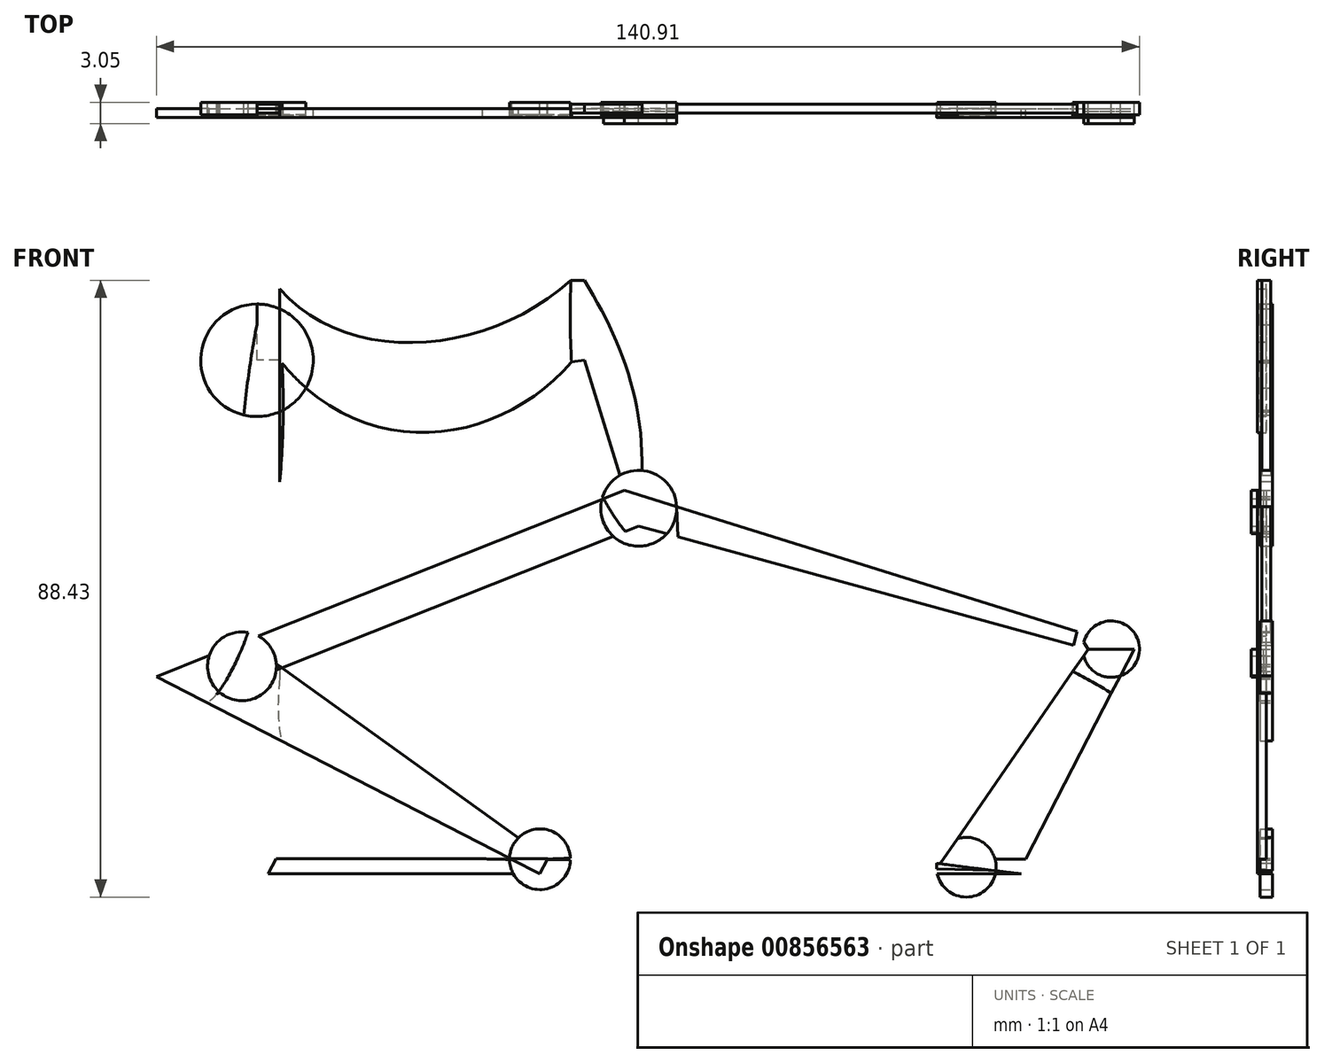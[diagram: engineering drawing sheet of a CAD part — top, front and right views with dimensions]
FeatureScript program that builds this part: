
annotation { "Feature Type Name" : "Feature", "Feature Type Description" : "" }
export const myFeature = defineFeature(function(context is Context, id is Id, definition is map)
    precondition{}
    {
        {
            var Q0;
            Q0=qCreatedBy(makeId("Front.planeOp"),FACE);
            var sketch = newSketch(context, id + "F0", { "sketchPlane" : qUnion([Q0])});
            skLineSegment(sketch, "E0", {"start": v(-61.65, 70.37) * mm, "end": v(-61.65, 0) * mm});
            skFitSpline(sketch, "E1", {"points": [v(-61.65, 0) * mm, v(-26.78, -25.9) * mm, v(7.97, -24.21) * mm, v(44.58, -27.97) * mm, v(64.47, -26.74) * mm, v(71.94, -19.1) * mm, v(70.5, -13.3) * mm, v(44.7, 4.15) * mm, v(0, 12.67) * mm, v(-18.49, 35.05) * mm, v(-18.6, 75.27) * mm], "startDerivative": vector(-64.2, -574.15) * mm, "endDerivative": vector(16.77, 189.29) * mm});
            skFitSpline(sketch, "E2", {"points": [v(-61.65, 55.92) * mm, v(-19.91, 57.13) * mm], "startDerivative": vector(29.36, -33.67) * mm, "endDerivative": vector(36.1, 32.54) * mm});
            skFitSpline(sketch, "E3", {"points": [v(-61.65, 45.68) * mm, v(-19.82, 45.43) * mm], "startDerivative": vector(37.74, -46.8) * mm, "endDerivative": vector(29.91, 34.83) * mm});
            skLineSegment(sketch, "E4", {"start": v(-61.65, 45.68) * mm, "end": v(-64.9, 45.68) * mm});
            skLineSegment(sketch, "E5", {"start": v(-64.9, 45.68) * mm, "end": v(-64.9, 55.92) * mm});
            skLineSegment(sketch, "E6", {"start": v(-64.9, 55.92) * mm, "end": v(-61.65, 55.92) * mm});
            skLineSegment(sketch, "E7", {"start": v(-19.91, 57.13) * mm, "end": v(-17.99, 57.13) * mm});
            skLineSegment(sketch, "E8", {"start": v(-17.99, 57.13) * mm, "end": v(-17.99, 45.68) * mm});
            skLineSegment(sketch, "E9", {"start": v(-17.99, 45.68) * mm, "end": v(-19.82, 45.43) * mm});
            skFitSpline(sketch, "E10", {"points": [v(-64.9, 50.8) * mm, v(-79.63, 0) * mm], "startDerivative": vector(-10.54, -51.15) * mm, "endDerivative": vector(-39.02, -39.29) * mm});
            skFitSpline(sketch, "E11", {"points": [v(-61.73, 50.8) * mm, v(-70.66, -2.16) * mm, v(-79.63, 0) * mm], "startDerivative": vector(10.97, -108.7) * mm, "endDerivative": vector(-50.85, 48.8) * mm});
            skLineSegment(sketch, "E12", {"start": v(-70.66, -2.16) * mm, "end": v(-10.18, 21.9) * mm});
            skLineSegment(sketch, "E13", {"start": v(-10.18, 21.9) * mm, "end": v(-12.22, 27.02) * mm});
            skLineSegment(sketch, "E14", {"start": v(-12.22, 27.02) * mm, "end": v(-79.32, 0.32) * mm});
            skLineSegment(sketch, "E15", {"start": v(-79.32, 0.32) * mm, "end": v(-24.34, -27.97) * mm});
            skLineSegment(sketch, "E16", {"start": v(-24.34, -27.97) * mm, "end": v(-23.23, -25.8) * mm});
            skLineSegment(sketch, "E17", {"start": v(-23.23, -25.8) * mm, "end": v(-66.66, 5.36) * mm});
            skLineSegment(sketch, "E18", {"start": v(-23.23, -25.8) * mm, "end": v(-62.17, -25.8) * mm});
            skLineSegment(sketch, "E19", {"start": v(-62.17, -25.8) * mm, "end": v(-63.28, -27.97) * mm});
            skLineSegment(sketch, "E20", {"start": v(-63.28, -27.97) * mm, "end": v(-23.23, -27.97) * mm});
            skLineSegment(sketch, "E21", {"start": v(-23.23, -27.97) * mm, "end": v(60.88, -27.97) * mm});
            skLineSegment(sketch, "E22", {"start": v(60.88, -27.97) * mm, "end": v(-24.34, -25.87) * mm});
            skLineSegment(sketch, "E23", {"start": v(-24.34, -25.87) * mm, "end": v(61.59, -25.87) * mm});
            skLineSegment(sketch, "E24", {"start": v(61.59, -25.87) * mm, "end": v(60.88, -27.97) * mm});
            skLineSegment(sketch, "E25", {"start": v(33.01, -26.53) * mm, "end": v(54.26, 4.25) * mm});
            skLineSegment(sketch, "E26", {"start": v(45.32, -25.87) * mm, "end": v(60.82, 4.25) * mm});
            skLineSegment(sketch, "E27", {"start": v(60.82, 4.25) * mm, "end": v(-12.22, 27.02) * mm});
            skLineSegment(sketch, "E28", {"start": v(-10.18, 21.9) * mm, "end": v(54.26, 4.25) * mm});
            skLineSegment(sketch, "E29", {"start": v(54.26, 4.25) * mm, "end": v(60.82, 4.25) * mm});
            skCircle(sketch, "E30", {"center": v(-67.05, 1.8) * mm, "radius": 4.93 * mm});
            skCircle(sketch, "E31", {"center": v(-10.18, 24.46) * mm, "radius": 5.44 * mm});
            skPoint(sketch, "E31.centerSnap0", {"position": v(-11.2, 24.46) * mm});
            skCircle(sketch, "E32", {"center": v(57.54, 4.25) * mm, "radius": 4.05 * mm});
            skCircle(sketch, "E33", {"center": v(-24.34, -25.87) * mm, "radius": 4.36 * mm});
            skCircle(sketch, "E34", {"center": v(36.78, -27.02) * mm, "radius": 4.28 * mm});
            skCircle(sketch, "E35", {"center": v(-64.9, 45.68) * mm, "radius": 8.06 * mm});
            skFitSpline(sketch, "E36", {"points": [v(-17.99, 57.13) * mm, v(-10.18, 24.46) * mm], "startDerivative": vector(17.67, -28.59) * mm, "endDerivative": vector(-5.48, -39.2) * mm});
            skFitSpline(sketch, "E37", {"points": [v(-17.99, 45.68) * mm, v(-12.22, 27.02) * mm], "startDerivative": vector(5.77, -18.66) * mm, "endDerivative": vector(5.77, -18.66) * mm});
            skLineSegment(sketch, "E38", {"start": v(-4.75, 24.7) * mm, "end": v(-4.56, 20.36) * mm});
            skLineSegment(sketch, "E39", {"start": v(54.26, 4.25) * mm, "end": v(52.66, 6.8) * mm});
            skLineSegment(sketch, "E40", {"start": v(52.66, 6.8) * mm, "end": v(52.12, 4.84) * mm});
            skSolve(sketch);
        }
        {
            var Q0;
            {var subQ5=sQuery(id+"F0.wireOp",EDGE,"E4");Q0=makeQuery(id+"F0.imprint","IMPRINT",FACE,{"disambiguationData":[TD([[makeQuery(id+"F0.imprint","IMPRINT",EDGE,{"derivedFrom":subQ5}),1.0]])]});}
            var Q1;
            {var subQ0=sQuery(id+"F0.wireOp",EDGE,"E2");Q1=makeQuery(id+"F0.imprint","IMPRINT",FACE,{"disambiguationData":[TD([[makeQuery(id+"F0.imprint","IMPRINT",EDGE,{"derivedFrom":subQ0}),-1.0]])]});}
            var Q2;
            {var subQ1=sQuery(id+"F0.wireOp",EDGE,"E4");Q2=makeQuery(id+"F0.imprint","IMPRINT",FACE,{"disambiguationData":[TD([[makeQuery(id+"F0.imprint","IMPRINT",EDGE,{"derivedFrom":subQ1}),-1.0]])]});}
            var Q3;
            {var subQ0=sQuery(id+"F0.wireOp",EDGE,"E14");var subQ1=sQuery(id+"F0.wireOp",EDGE,"E0");var subQ2=makeQuery(id+"F0.imprint","INTERSECT",VERTEX,{"derivedFrom":[subQ1,subQ0]});Q3=makeQuery(id+"F0.imprint","IMPRINT",FACE,{"disambiguationData":[TD([[makeQuery(id+"F0.imprint","IMPRINT",EDGE,{"disambiguationData":[TD([[subQ2,-1.0]])],"derivedFrom":subQ1}),-1.0]])]});}
            var Q4;
            {var subQ0=sQuery(id+"F0.wireOp",EDGE,"E14");var subQ3=sQuery(id+"F0.wireOp",EDGE,"E0");var subQ4=makeQuery(id+"F0.imprint","INTERSECT",VERTEX,{"derivedFrom":[subQ3,subQ0]});Q4=makeQuery(id+"F0.imprint","IMPRINT",FACE,{"disambiguationData":[TD([[makeQuery(id+"F0.imprint","IMPRINT",EDGE,{"disambiguationData":[TD([[subQ4,-1.0]])],"derivedFrom":subQ3}),1.0]])]});}
            var Q5;
            {var subQ1=sQuery(id+"F0.wireOp",EDGE,"E1");var subQ6=sQuery(id+"F0.wireOp",EDGE,"E0");var subQ10=makeQuery(id+"F0.imprint","INTERSECT",VERTEX,{"derivedFrom":[subQ6,subQ1]});Q5=makeQuery(id+"F0.imprint","IMPRINT",FACE,{"disambiguationData":[TD([[makeQuery(id+"F0.imprint","IMPRINT",EDGE,{"disambiguationData":[TD([[subQ10,1.0]])],"derivedFrom":subQ6}),1.0]])]});}
            var Q6;
            {var subQ5=sQuery(id+"F0.wireOp",EDGE,"E1");var subQ6=sQuery(id+"F0.wireOp",EDGE,"E0");var subQ7=makeQuery(id+"F0.imprint","INTERSECT",VERTEX,{"derivedFrom":[subQ6,subQ5]});Q6=makeQuery(id+"F0.imprint","IMPRINT",FACE,{"disambiguationData":[TD([[makeQuery(id+"F0.imprint","IMPRINT",EDGE,{"disambiguationData":[TD([[subQ7,1.0]])],"derivedFrom":subQ6}),-1.0]])]});}
            var Q7;
            {var subQ0=sQuery(id+"F0.wireOp",EDGE,"E11");var subQ1=makeQuery(id+"F0.imprint","INTERSECT",VERTEX,{"derivedFrom":[subQ0,sQuery(id+"F0.wireOp",EDGE,"E12")]});Q7=makeQuery(id+"F0.imprint","IMPRINT",FACE,{"disambiguationData":[TD([[makeQuery(id+"F0.imprint","IMPRINT",EDGE,{"disambiguationData":[TD([[subQ1,-1.0]])],"derivedFrom":subQ0}),-1.0]])]});}
            var Q8;
            Q8=makeQuery(id+"F0.imprint","IMPRINT",FACE,{"disambiguationData":[TD([[makeQuery(id+"F0.imprint","IMPRINT",EDGE,{"derivedFrom":sQuery(id+"F0.wireOp",EDGE,"E13")}),-1.0]])]});
            var Q9;
            {var subQ5=sQuery(id+"F0.wireOp",EDGE,"E13");Q9=makeQuery(id+"F0.imprint","IMPRINT",FACE,{"disambiguationData":[TD([[makeQuery(id+"F0.imprint","IMPRINT",EDGE,{"derivedFrom":subQ5}),1.0]])]});}
            var Q10;
            {var subQ0=sQuery(id+"F0.wireOp",EDGE,"E26");var subQ1=sQuery(id+"F0.wireOp",EDGE,"E1");var subQ2=makeQuery(id+"F0.imprint","INTERSECT",VERTEX,{"derivedFrom":[subQ1,subQ0]});Q10=makeQuery(id+"F0.imprint","IMPRINT",FACE,{"disambiguationData":[TD([[makeQuery(id+"F0.imprint","IMPRINT",EDGE,{"disambiguationData":[TD([[subQ2,-1.0]])],"derivedFrom":subQ1}),1.0]])]});}
            var Q11;
            {var subQ5=sQuery(id+"F0.wireOp",EDGE,"E29");Q11=makeQuery(id+"F0.imprint","IMPRINT",FACE,{"disambiguationData":[TD([[makeQuery(id+"F0.imprint","IMPRINT",EDGE,{"derivedFrom":subQ5}),-1.0]])]});}
            var Q12;
            {var subQ0=sQuery(id+"F0.wireOp",EDGE,"E21");var subQ3=sQuery(id+"F0.wireOp",EDGE,"E1");var subQ4=makeQuery(id+"F0.imprint","INTERSECT",VERTEX,{"derivedFrom":[subQ3,subQ0]});Q12=makeQuery(id+"F0.imprint","IMPRINT",FACE,{"disambiguationData":[TD([[makeQuery(id+"F0.imprint","IMPRINT",EDGE,{"disambiguationData":[TD([[subQ4,1.0]])],"derivedFrom":subQ3}),-1.0]])]});}
            var Q13;
            {var subQ1=sQuery(id+"F0.wireOp",EDGE,"E1");var subQ7=makeQuery(id+"F0.imprint","INTERSECT",VERTEX,{"disambiguationData":[OD(0.0)],"derivedFrom":[subQ1,sQuery(id+"F0.wireOp",EDGE,"E25")]});Q13=makeQuery(id+"F0.imprint","IMPRINT",FACE,{"disambiguationData":[TD([[makeQuery(id+"F0.imprint","IMPRINT",EDGE,{"disambiguationData":[TD([[subQ7,1.0]])],"derivedFrom":subQ1}),-1.0]])]});}
            var Q14;
            {var subQ0=sQuery(id+"F0.wireOp",EDGE,"E19");Q14=makeQuery(id+"F0.imprint","IMPRINT",FACE,{"disambiguationData":[TD([[makeQuery(id+"F0.imprint","IMPRINT",EDGE,{"derivedFrom":subQ0}),1.0]])]});}
            extrude(context, id + "F1", {"entities" : qUnion([Q0, Q1, Q2, Q3, Q4, Q5, Q6, Q7, Q8, Q9, Q10, Q11, Q12, Q13, Q14]), "depth" : 1.27 * mm, "offsetDistance" : 25.4 * mm});
        }
        {
            var Q0;
            {var subQ0=sQuery(id+"F0.wireOp",EDGE,"E38");Q0=makeQuery(id+"F0.imprint","IMPRINT",FACE,{"disambiguationData":[TD([[makeQuery(id+"F0.imprint","IMPRINT",EDGE,{"derivedFrom":subQ0}),1.0]])]});}
            var Q1;
            {var subQ0=sQuery(id+"F0.wireOp",EDGE,"E8");Q1=makeQuery(id+"F0.imprint","IMPRINT",FACE,{"disambiguationData":[TD([[makeQuery(id+"F0.imprint","IMPRINT",EDGE,{"derivedFrom":subQ0}),1.0]])]});}
            var Q2;
            {var subQ0=sQuery(id+"F0.wireOp",EDGE,"E7");Q2=makeQuery(id+"F0.imprint","IMPRINT",FACE,{"disambiguationData":[TD([[makeQuery(id+"F0.imprint","IMPRINT",EDGE,{"derivedFrom":subQ0}),-1.0]])]});}
            var Q3;
            {var subQ6=sQuery(id+"F0.wireOp",EDGE,"E0");var subQ9=sQuery(id+"F0.wireOp",EDGE,"E35");var subQ11=makeQuery(id+"F0.imprint","INTERSECT",VERTEX,{"disambiguationData":[OD(1.0)],"derivedFrom":[subQ6,subQ9]});Q3=makeQuery(id+"F0.imprint","IMPRINT",FACE,{"disambiguationData":[TD([[makeQuery(id+"F0.imprint","IMPRINT",EDGE,{"disambiguationData":[TD([[subQ11,-1.0]])],"derivedFrom":subQ6}),-1.0]])]});}
            extrude(context, id + "F2", {"entities" : qUnion([Q0, Q1, Q2, Q3]), "endBound" : BoundingType.SYMMETRIC, "depth" : 1.27 * mm, "offsetDistance" : 25.4 * mm});
        }
        {
            var Q0;
            {var subQ0=sQuery(id+"F0.wireOp",EDGE,"E10");var subQ1=sQuery(id+"F0.wireOp",EDGE,"E5");var subQ2=makeQuery(id+"F0.imprint","INTERSECT",VERTEX,{"derivedFrom":[subQ1,subQ0]});Q0=makeQuery(id+"F0.imprint","IMPRINT",FACE,{"disambiguationData":[TD([[makeQuery(id+"F0.imprint","IMPRINT",EDGE,{"disambiguationData":[TD([[subQ2,-1.0]])],"derivedFrom":subQ1}),1.0]])]});}
            var Q1;
            {var subQ0=sQuery(id+"F0.wireOp",EDGE,"E11");var subQ1=sQuery(id+"F0.wireOp",EDGE,"E0");var subQ2=makeQuery(id+"F0.imprint","INTERSECT",VERTEX,{"disambiguationData":[OD(0.0)],"derivedFrom":[subQ1,subQ0]});Q1=makeQuery(id+"F0.imprint","IMPRINT",FACE,{"disambiguationData":[TD([[makeQuery(id+"F0.imprint","IMPRINT",EDGE,{"disambiguationData":[TD([[subQ2,1.0]])],"derivedFrom":subQ1}),1.0]])]});}
            var Q2;
            {var subQ0=sQuery(id+"F0.wireOp",EDGE,"E11");var subQ1=sQuery(id+"F0.wireOp",EDGE,"E3");var subQ2=makeQuery(id+"F0.imprint","INTERSECT",VERTEX,{"derivedFrom":[subQ1,subQ0]});Q2=makeQuery(id+"F0.imprint","IMPRINT",FACE,{"disambiguationData":[TD([[makeQuery(id+"F0.imprint","IMPRINT",EDGE,{"disambiguationData":[TD([[subQ2,-1.0]])],"derivedFrom":subQ1}),-1.0]])]});}
            var Q3;
            {var subQ1=sQuery(id+"F0.wireOp",EDGE,"E11");var subQ3=sQuery(id+"F0.wireOp",EDGE,"E30");var subQ4=makeQuery(id+"F0.imprint","INTERSECT",VERTEX,{"disambiguationData":[OD(1.0)],"derivedFrom":[subQ1,subQ3]});Q3=makeQuery(id+"F0.imprint","IMPRINT",FACE,{"disambiguationData":[TD([[makeQuery(id+"F0.imprint","IMPRINT",EDGE,{"disambiguationData":[TD([[subQ4,1.0]])],"derivedFrom":subQ3}),1.0]])]});}
            var Q4;
            {var subQ1=sQuery(id+"F0.wireOp",EDGE,"E11");var subQ3=sQuery(id+"F0.wireOp",EDGE,"E30");var subQ4=makeQuery(id+"F0.imprint","INTERSECT",VERTEX,{"disambiguationData":[OD(0.0)],"derivedFrom":[subQ1,subQ3]});Q4=makeQuery(id+"F0.imprint","IMPRINT",FACE,{"disambiguationData":[TD([[makeQuery(id+"F0.imprint","IMPRINT",EDGE,{"disambiguationData":[TD([[subQ4,-1.0]])],"derivedFrom":subQ3}),1.0]])]});}
            var Q5;
            {var subQ3=sQuery(id+"F0.wireOp",EDGE,"E30");var subQ6=sQuery(id+"F0.wireOp",EDGE,"E12");var subQ7=makeQuery(id+"F0.imprint","INTERSECT",VERTEX,{"disambiguationData":[OD(0.0)],"derivedFrom":[subQ6,subQ3]});Q5=makeQuery(id+"F0.imprint","IMPRINT",FACE,{"disambiguationData":[TD([[makeQuery(id+"F0.imprint","IMPRINT",EDGE,{"disambiguationData":[TD([[subQ7,-1.0]])],"derivedFrom":subQ6}),1.0]])]});}
            var Q6;
            {var subQ1=sQuery(id+"F0.wireOp",EDGE,"E14");var subQ3=sQuery(id+"F0.wireOp",EDGE,"E30");var subQ4=makeQuery(id+"F0.imprint","INTERSECT",VERTEX,{"disambiguationData":[OD(0.0)],"derivedFrom":[subQ1,subQ3]});Q6=makeQuery(id+"F0.imprint","IMPRINT",FACE,{"disambiguationData":[TD([[makeQuery(id+"F0.imprint","IMPRINT",EDGE,{"disambiguationData":[TD([[subQ4,1.0]])],"derivedFrom":subQ3}),1.0]])]});}
            var Q7;
            {var subQ0=sQuery(id+"F0.wireOp",EDGE,"E30");var subQ1=sQuery(id+"F0.wireOp",EDGE,"E12");var subQ2=makeQuery(id+"F0.imprint","INTERSECT",VERTEX,{"disambiguationData":[OD(0.0)],"derivedFrom":[subQ1,subQ0]});Q7=makeQuery(id+"F0.imprint","IMPRINT",FACE,{"disambiguationData":[TD([[makeQuery(id+"F0.imprint","IMPRINT",EDGE,{"disambiguationData":[TD([[subQ2,-1.0]])],"derivedFrom":subQ1}),-1.0]])]});}
            var Q8;
            {var subQ0=sQuery(id+"F0.wireOp",EDGE,"E31");var subQ1=sQuery(id+"F0.wireOp",EDGE,"E1");var subQ2=makeQuery(id+"F0.imprint","INTERSECT",VERTEX,{"disambiguationData":[OD(0.0)],"derivedFrom":[subQ1,subQ0]});Q8=makeQuery(id+"F0.imprint","IMPRINT",FACE,{"disambiguationData":[TD([[makeQuery(id+"F0.imprint","IMPRINT",EDGE,{"disambiguationData":[TD([[subQ2,-1.0]])],"derivedFrom":subQ1}),-1.0]])]});}
            var Q9;
            {var subQ1=sQuery(id+"F0.wireOp",EDGE,"E27");var subQ3=sQuery(id+"F0.wireOp",EDGE,"E36");var subQ4=makeQuery(id+"F0.imprint","INTERSECT",VERTEX,{"derivedFrom":[subQ1,subQ3]});Q9=makeQuery(id+"F0.imprint","IMPRINT",FACE,{"disambiguationData":[TD([[makeQuery(id+"F0.imprint","IMPRINT",EDGE,{"disambiguationData":[TD([[subQ4,1.0]])],"derivedFrom":subQ3}),1.0]])]});}
            var Q10;
            {var subQ3=sQuery(id+"F0.wireOp",EDGE,"E36");var subQ5=sQuery(id+"F0.wireOp",EDGE,"E31");var subQ6=makeQuery(id+"F0.imprint","INTERSECT",VERTEX,{"derivedFrom":[subQ5,subQ3]});Q10=makeQuery(id+"F0.imprint","IMPRINT",FACE,{"disambiguationData":[TD([[makeQuery(id+"F0.imprint","IMPRINT",EDGE,{"disambiguationData":[TD([[subQ6,-1.0]])],"derivedFrom":subQ5}),1.0]])]});}
            var Q11;
            {var subQ0=sQuery(id+"F0.wireOp",EDGE,"E12");var subQ1=sQuery(id+"F0.wireOp",EDGE,"E1");var subQ2=makeQuery(id+"F0.imprint","INTERSECT",VERTEX,{"derivedFrom":[subQ1,subQ0]});Q11=makeQuery(id+"F0.imprint","IMPRINT",FACE,{"disambiguationData":[TD([[makeQuery(id+"F0.imprint","IMPRINT",EDGE,{"disambiguationData":[TD([[subQ2,-1.0]])],"derivedFrom":subQ1}),1.0]])]});}
            var Q12;
            Q12=makeQuery(id+"F1.opExtrude","CAP_FACE",FACE,{"disambiguationData":[OSD([sQuery(id+"F0.wireOp",EDGE,"E1"),sQuery(id+"F0.wireOp",EDGE,"E12"),sQuery(id+"F0.wireOp",EDGE,"E14"),sQuery(id+"F0.wireOp",EDGE,"E27"),sQuery(id+"F0.wireOp",EDGE,"E28"),sQuery(id+"F0.wireOp",EDGE,"E31")])],"isStart":false});
            var Q13;
            {var subQ0=sQuery(id+"F0.wireOp",EDGE,"E14");var subQ1=sQuery(id+"F0.wireOp",EDGE,"E1");var subQ2=makeQuery(id+"F0.imprint","INTERSECT",VERTEX,{"derivedFrom":[subQ1,subQ0]});Q13=makeQuery(id+"F0.imprint","IMPRINT",FACE,{"disambiguationData":[TD([[makeQuery(id+"F0.imprint","IMPRINT",EDGE,{"disambiguationData":[TD([[subQ2,-1.0]])],"derivedFrom":subQ1}),-1.0]])]});}
            var Q14;
            {var subQ0=sQuery(id+"F0.wireOp",EDGE,"E31");var subQ1=sQuery(id+"F0.wireOp",EDGE,"E1");var subQ2=makeQuery(id+"F0.imprint","INTERSECT",VERTEX,{"disambiguationData":[OD(0.0)],"derivedFrom":[subQ1,subQ0]});Q14=makeQuery(id+"F0.imprint","IMPRINT",FACE,{"disambiguationData":[TD([[makeQuery(id+"F0.imprint","IMPRINT",EDGE,{"disambiguationData":[TD([[subQ2,-1.0]])],"derivedFrom":subQ1}),1.0]])]});}
            var Q15;
            {var subQ0=sQuery(id+"F0.wireOp",EDGE,"E16");var subQ1=sQuery(id+"F0.wireOp",EDGE,"E1");var subQ2=makeQuery(id+"F0.imprint","INTERSECT",VERTEX,{"derivedFrom":[subQ1,subQ0]});Q15=makeQuery(id+"F0.imprint","IMPRINT",FACE,{"disambiguationData":[TD([[makeQuery(id+"F0.imprint","IMPRINT",EDGE,{"disambiguationData":[TD([[subQ2,-1.0]])],"derivedFrom":subQ1}),1.0]])]});}
            var Q16;
            {var subQ0=sQuery(id+"F0.wireOp",EDGE,"E33");var subQ1=sQuery(id+"F0.wireOp",EDGE,"E15");var subQ2=makeQuery(id+"F0.imprint","INTERSECT",VERTEX,{"derivedFrom":[subQ1,subQ0]});Q16=makeQuery(id+"F0.imprint","IMPRINT",FACE,{"disambiguationData":[TD([[makeQuery(id+"F0.imprint","IMPRINT",EDGE,{"disambiguationData":[TD([[subQ2,-1.0]])],"derivedFrom":subQ1}),1.0]])]});}
            var Q17;
            {var subQ0=sQuery(id+"F0.wireOp",EDGE,"E20");var subQ4=sQuery(id+"F0.wireOp",EDGE,"E21");var subQ5=makeQuery(id+"F0.imprint","INTERSECT",VERTEX,{"derivedFrom":[subQ0,subQ4]});Q17=makeQuery(id+"F0.imprint","IMPRINT",FACE,{"disambiguationData":[TD([[makeQuery(id+"F0.imprint","IMPRINT",EDGE,{"disambiguationData":[TD([[subQ5,-1.0]])],"derivedFrom":subQ4}),-1.0]])]});}
            var Q18;
            {var subQ0=sQuery(id+"F0.wireOp",EDGE,"E21");var subQ1=sQuery(id+"F0.wireOp",EDGE,"E20");var subQ2=makeQuery(id+"F0.imprint","INTERSECT",VERTEX,{"derivedFrom":[subQ1,subQ0]});Q18=makeQuery(id+"F0.imprint","IMPRINT",FACE,{"disambiguationData":[TD([[makeQuery(id+"F0.imprint","IMPRINT",EDGE,{"disambiguationData":[TD([[subQ2,-1.0]])],"derivedFrom":subQ0}),1.0]])]});}
            var Q19;
            {var subQ0=sQuery(id+"F0.wireOp",EDGE,"E33");var subQ1=sQuery(id+"F0.wireOp",EDGE,"E1");var subQ2=makeQuery(id+"F0.imprint","INTERSECT",VERTEX,{"disambiguationData":[OD(0.0)],"derivedFrom":[subQ1,subQ0]});Q19=makeQuery(id+"F0.imprint","IMPRINT",FACE,{"disambiguationData":[TD([[makeQuery(id+"F0.imprint","IMPRINT",EDGE,{"disambiguationData":[TD([[subQ2,-1.0]])],"derivedFrom":subQ1}),-1.0]])]});}
            var Q20;
            {var subQ0=sQuery(id+"F0.wireOp",EDGE,"E34");var subQ1=sQuery(id+"F0.wireOp",EDGE,"E21");var subQ2=makeQuery(id+"F0.imprint","INTERSECT",VERTEX,{"disambiguationData":[OD(0.0)],"derivedFrom":[subQ1,subQ0]});Q20=makeQuery(id+"F0.imprint","IMPRINT",FACE,{"disambiguationData":[TD([[makeQuery(id+"F0.imprint","IMPRINT",EDGE,{"disambiguationData":[TD([[subQ2,-1.0]])],"derivedFrom":subQ1}),-1.0]])]});}
            var Q21;
            {var subQ0=sQuery(id+"F0.wireOp",EDGE,"E25");var subQ1=sQuery(id+"F0.wireOp",EDGE,"E23");var subQ2=makeQuery(id+"F0.imprint","INTERSECT",VERTEX,{"derivedFrom":[subQ1,subQ0]});Q21=makeQuery(id+"F0.imprint","IMPRINT",FACE,{"disambiguationData":[TD([[makeQuery(id+"F0.imprint","IMPRINT",EDGE,{"disambiguationData":[TD([[subQ2,-1.0]])],"derivedFrom":subQ1}),1.0]])]});}
            var Q22;
            {var subQ0=sQuery(id+"F0.wireOp",EDGE,"E25");var subQ1=sQuery(id+"F0.wireOp",EDGE,"E1");var subQ2=makeQuery(id+"F0.imprint","INTERSECT",VERTEX,{"disambiguationData":[OD(0.0)],"derivedFrom":[subQ1,subQ0]});Q22=makeQuery(id+"F0.imprint","IMPRINT",FACE,{"disambiguationData":[TD([[makeQuery(id+"F0.imprint","IMPRINT",EDGE,{"disambiguationData":[TD([[subQ2,-1.0]])],"derivedFrom":subQ1}),1.0]])]});}
            var Q23;
            {var subQ0=sQuery(id+"F0.wireOp",EDGE,"E29");Q23=makeQuery(id+"F0.imprint","IMPRINT",FACE,{"disambiguationData":[TD([[makeQuery(id+"F0.imprint","IMPRINT",EDGE,{"derivedFrom":subQ0}),1.0]])]});}
            var Q24;
            {var subQ1=sQuery(id+"F0.wireOp",EDGE,"E26");var subQ3=sQuery(id+"F0.wireOp",EDGE,"E32");var subQ4=makeQuery(id+"F0.imprint","INTERSECT",VERTEX,{"derivedFrom":[subQ1,subQ3]});Q24=makeQuery(id+"F0.imprint","IMPRINT",FACE,{"disambiguationData":[TD([[makeQuery(id+"F0.imprint","IMPRINT",EDGE,{"disambiguationData":[TD([[subQ4,-1.0]])],"derivedFrom":subQ3}),1.0]])]});}
            var Q25;
            {var subQ0=sQuery(id+"F0.wireOp",EDGE,"E26");var subQ1=sQuery(id+"F0.wireOp",EDGE,"E1");var subQ2=makeQuery(id+"F0.imprint","INTERSECT",VERTEX,{"derivedFrom":[subQ1,subQ0]});Q25=makeQuery(id+"F0.imprint","IMPRINT",FACE,{"disambiguationData":[TD([[makeQuery(id+"F0.imprint","IMPRINT",EDGE,{"disambiguationData":[TD([[subQ2,-1.0]])],"derivedFrom":subQ1}),-1.0]])]});}
            var Q26;
            Q26=makeQuery(id+"F1.opExtrude","CAP_FACE",FACE,{"disambiguationData":[OSD([sQuery(id+"F0.wireOp",EDGE,"E25"),sQuery(id+"F0.wireOp",EDGE,"E26"),sQuery(id+"F0.wireOp",EDGE,"E29"),sQuery(id+"F0.wireOp",EDGE,"E32")])],"isStart":false});
            extrude(context, id + "F3", {"entities" : qUnion([Q0, Q1, Q2, Q3, Q4, Q5, Q6, Q7, Q8, Q9, Q10, Q11, Q12, Q13, Q14, Q15, Q16, Q17, Q18, Q19, Q20, Q21, Q22, Q23, Q24, Q25, Q26]), "endBound" : BoundingType.SYMMETRIC, "depth" : 1.78 * mm, "offsetDistance" : 25.4 * mm});
        }
    });
